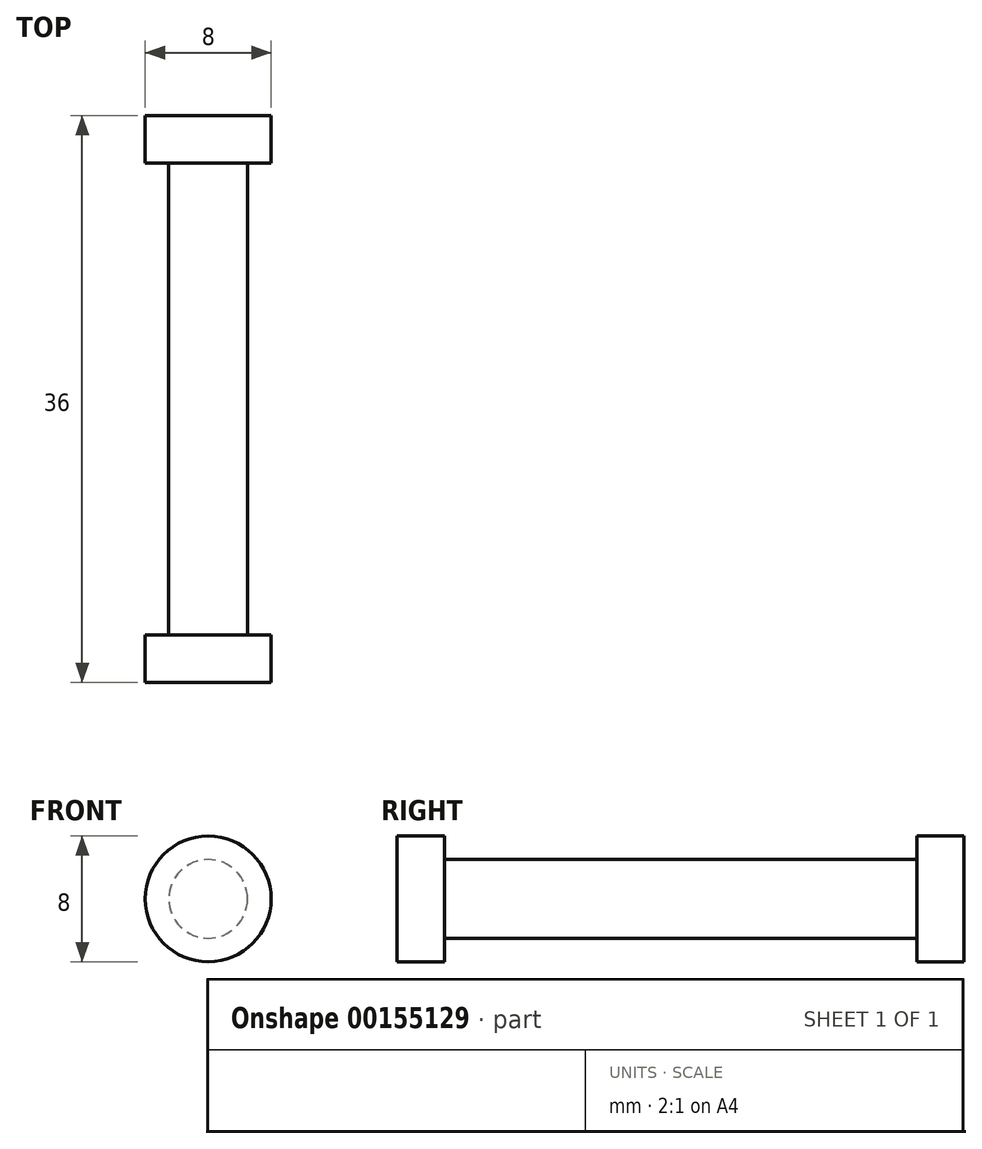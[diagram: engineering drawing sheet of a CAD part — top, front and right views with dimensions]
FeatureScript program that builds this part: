
annotation { "Feature Type Name" : "Feature", "Feature Type Description" : "" }
export const myFeature = defineFeature(function(context is Context, id is Id, definition is map)
    precondition{}
    {
        {
            var Q0;
            Q0=qCreatedBy(makeId("Front.planeOp"),FACE);
            var sketch = newSketch(context, id + "F0", { "sketchPlane" : qUnion([Q0])});
            skCircle(sketch, "E0", {"center": v(0, 0) * mm, "radius": 4 * mm});
            skSolve(sketch);
        }
        {
            var Q0;
            Q0=makeQuery(id+"F0.imprint","IMPRINT",FACE,{"disambiguationData":[TD([[makeQuery(id+"F0.imprint","IMPRINT",EDGE,{"derivedFrom":sQuery(id+"F0.wireOp",EDGE,"E0")}),1.0]])]});
            extrude(context, id + "F1", {"entities" : qUnion([Q0]), "depth" : 3 * mm});
        }
        {
            var Q0;
            Q0=makeQuery(id+"F1.opExtrude","CAP_FACE",FACE,{"disambiguationData":[OSD([sQuery(id+"F0.wireOp",EDGE,"E0")])],"isStart":false});
            var sketch = newSketch(context, id + "F2", { "sketchPlane" : qUnion([Q0])});
            skCircle(sketch, "E1", {"center": v(0, 0) * mm, "radius": 2.5 * mm});
            skSolve(sketch);
        }
        {
            var Q0;
            Q0=makeQuery(id+"F2.imprint","IMPRINT",FACE,{"disambiguationData":[TD([[makeQuery(id+"F2.imprint","IMPRINT",EDGE,{"derivedFrom":sQuery(id+"F2.wireOp",EDGE,"E1")}),1.0]])]});
            extrude(context, id + "F3", {"entities" : qUnion([Q0]), "operationType" : NewBodyOperationType.ADD, "depth" : 30 * mm});
        }
        {
            var Q0;
            Q0=makeQuery(id+"F3.opExtrude","CAP_FACE",FACE,{"disambiguationData":[OSD([sQuery(id+"F2.wireOp",EDGE,"E1")])],"isStart":false});
            var sketch = newSketch(context, id + "F4", { "sketchPlane" : qUnion([Q0])});
            skCircle(sketch, "E2", {"center": v(0, 0) * mm, "radius": 4 * mm});
            skSolve(sketch);
        }
        {
            var Q0;
            Q0=makeQuery(id+"F4.imprint","IMPRINT",FACE,{"disambiguationData":[TD([[makeQuery(id+"F4.imprint","IMPRINT",EDGE,{"derivedFrom":makeQuery(id+"F3.opExtrude","CAP_EDGE",EDGE,{"disambiguationData":[OSD([sQuery(id+"F2.wireOp",EDGE,"E1")])],"isStart":false})}),1.0]])]});
            var Q1;
            Q1=makeQuery(id+"F4.imprint","IMPRINT",FACE,{"disambiguationData":[TD([[makeQuery(id+"F4.imprint","IMPRINT",EDGE,{"derivedFrom":sQuery(id+"F4.wireOp",EDGE,"E2")}),1.0]])]});
            extrude(context, id + "F5", {"entities" : qUnion([Q0, Q1]), "operationType" : NewBodyOperationType.ADD, "depth" : 3 * mm});
        }
    });
